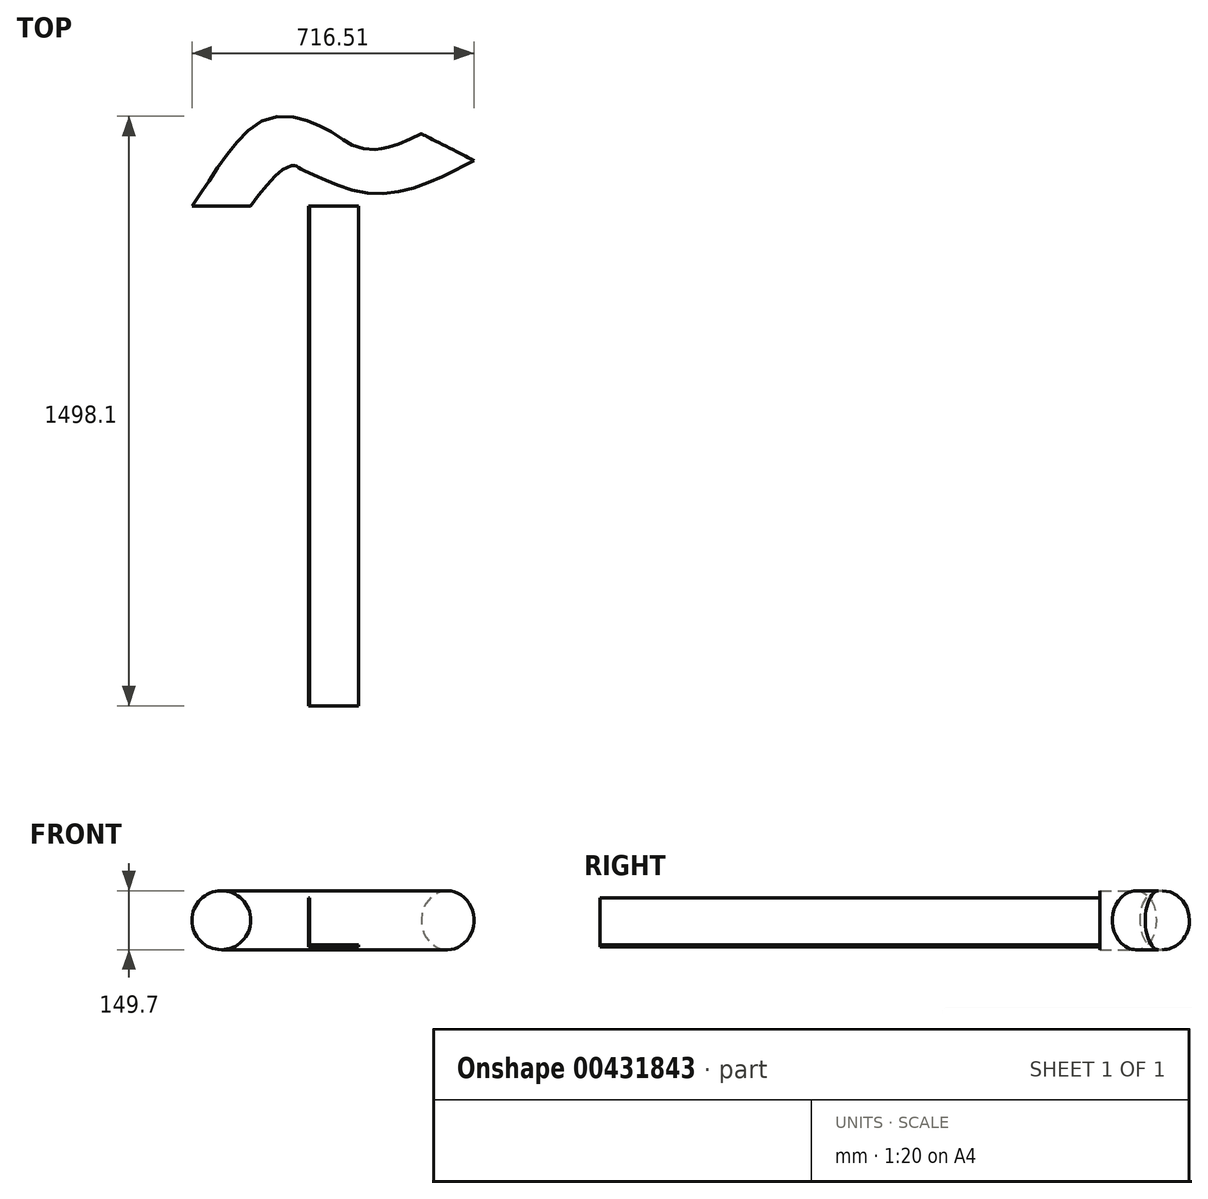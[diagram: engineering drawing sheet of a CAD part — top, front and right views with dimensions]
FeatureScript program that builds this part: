
annotation { "Feature Type Name" : "Feature", "Feature Type Description" : "" }
export const myFeature = defineFeature(function(context is Context, id is Id, definition is map)
    precondition{}
    {
        {
            var Q0;
            Q0=qCreatedBy(makeId("Front.planeOp"),FACE);
            var sketch = newSketch(context, id + "F0", { "sketchPlane" : qUnion([Q0])});
            skLineSegment(sketch, "E0.bottom", {"start": v(-68.96, 56.84) * mm, "end": v(-65.7, 56.84) * mm});
            skLineSegment(sketch, "E0.top", {"start": v(-68.96, -68.03) * mm, "end": v(-65.7, -68.03) * mm});
            skLineSegment(sketch, "E0.left", {"start": v(-68.96, 56.84) * mm, "end": v(-68.96, -68.03) * mm});
            skLineSegment(sketch, "E0.right", {"start": v(-65.7, 56.84) * mm, "end": v(-65.7, -68.03) * mm});
            skLineSegment(sketch, "E1.bottom", {"start": v(-65.7, -68.03) * mm, "end": v(58.7, -68.03) * mm});
            skLineSegment(sketch, "E1.top", {"start": v(-65.7, -61.97) * mm, "end": v(58.7, -61.97) * mm});
            skLineSegment(sketch, "E1.left", {"start": v(-65.7, -68.03) * mm, "end": v(-65.7, -61.97) * mm});
            skLineSegment(sketch, "E1.right", {"start": v(58.7, -68.03) * mm, "end": v(58.7, -61.97) * mm});
            skLineSegment(sketch, "E2.bottom", {"start": v(58.7, -61.97) * mm, "end": v(53.12, -61.97) * mm});
            skLineSegment(sketch, "E2.top", {"start": v(58.7, 57.78) * mm, "end": v(53.12, 57.78) * mm});
            skLineSegment(sketch, "E2.left", {"start": v(58.7, -61.97) * mm, "end": v(58.7, 57.78) * mm});
            skLineSegment(sketch, "E2.right", {"start": v(53.12, -61.97) * mm, "end": v(53.12, 57.78) * mm});
            skSolve(sketch);
        }
        {
            var Q0;
            Q0=makeQuery(id+"F0.imprint","IMPRINT",FACE,{"disambiguationData":[TD([[makeQuery(id+"F0.imprint","IMPRINT",EDGE,{"derivedFrom":sQuery(id+"F0.wireOp",EDGE,"E0.bottom")}),-1.0]])]});
            var Q1;
            Q1=makeQuery(id+"F0.imprint","IMPRINT",FACE,{"disambiguationData":[TD([[makeQuery(id+"F0.imprint","IMPRINT",EDGE,{"derivedFrom":sQuery(id+"F0.wireOp",EDGE,"E1.bottom")}),1.0]])]});
            var Q2;
            Q2=makeQuery(id+"F0.imprint","IMPRINT",FACE,{"disambiguationData":[TD([[makeQuery(id+"F0.imprint","IMPRINT",EDGE,{"derivedFrom":sQuery(id+"F0.wireOp",EDGE,"E2.bottom")}),-1.0]])]});
            extrude(context, id + "F1", {"entities" : qUnion([Q0, Q1, Q2]), "depth" : 1270 * mm});
        }
        {
            var Q0;
            Q0=qCreatedBy(makeId("Top.planeOp"),FACE);
            var sketch = newSketch(context, id + "F2", { "sketchPlane" : qUnion([Q0])});
            skFitSpline(sketch, "E3", {"points": [v(-285.98, 23.72) * mm, v(-125.2, 167.37) * mm, v(81.7, 105.43) * mm, v(299.15, 168.69) * mm], "startDerivative": vector(450.53, 624.89) * mm, "endDerivative": vector(637.04, 329.53) * mm});
            skSolve(sketch);
        }
        {
            var Q0;
            Q0=qCreatedBy(makeId("Front.planeOp"),FACE);
            var sketch = newSketch(context, id + "F3", { "sketchPlane" : qUnion([Q0])});
            skCircle(sketch, "E4", {"center": v(-290.37, 0) * mm, "radius": 74.85 * mm});
            skSolve(sketch);
        }
        {
            var Q0;
            Q0=makeQuery(id+"F3.imprint","IMPRINT",FACE,{"disambiguationData":[TD([[makeQuery(id+"F3.imprint","IMPRINT",EDGE,{"derivedFrom":sQuery(id+"F3.wireOp",EDGE,"E4")}),1.0]])]});
            var Q1;
            Q1=sQuery(id+"F2.wireOp",EDGE,"E3");
            sweep(context, id + "F4", {"profiles" : qUnion([Q0]), "path" : qUnion([Q1])});
        }
    });
